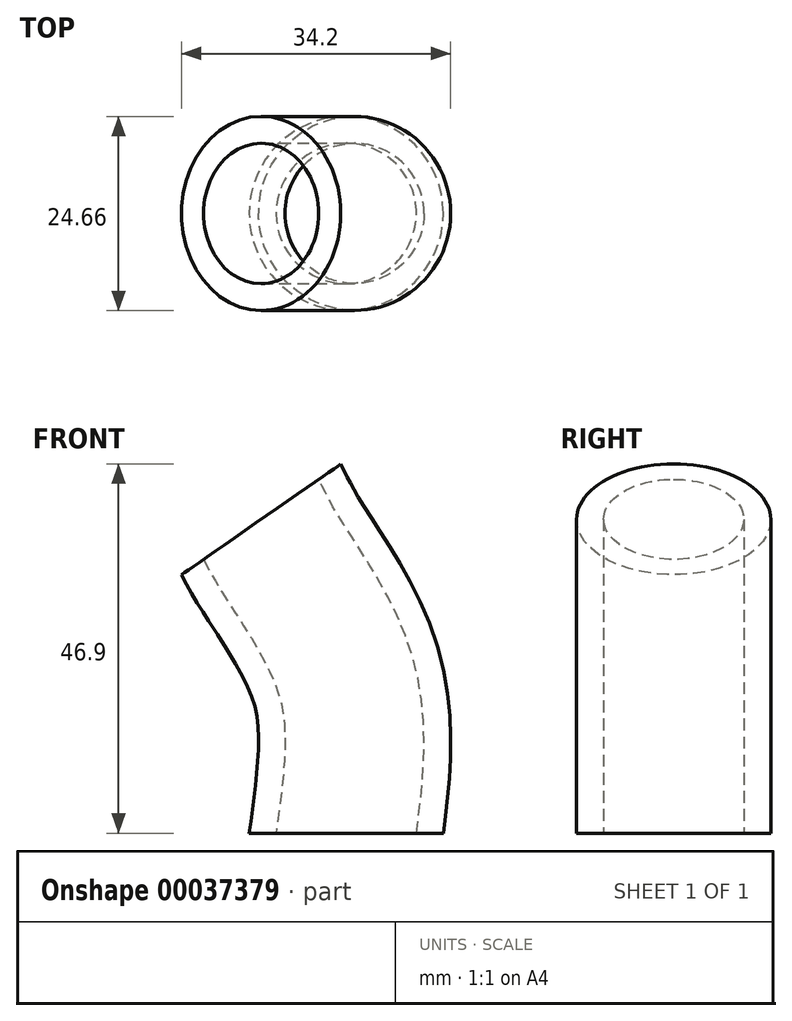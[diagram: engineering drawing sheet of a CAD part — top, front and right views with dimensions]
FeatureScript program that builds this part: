
annotation { "Feature Type Name" : "Feature", "Feature Type Description" : "" }
export const myFeature = defineFeature(function(context is Context, id is Id, definition is map)
    precondition{}
    {
        {
            var Q0;
            Q0=qCreatedBy(makeId("Top.planeOp"),FACE);
            var sketch = newSketch(context, id + "F0", { "sketchPlane" : qUnion([Q0])});
            skCircle(sketch, "E0", {"center": v(0, 0) * mm, "radius": 8.91 * mm});
            skCircle(sketch, "E1", {"center": v(0, 0) * mm, "radius": 12.33 * mm});
            skSolve(sketch);
        }
        {
            var Q0;
            Q0=qCreatedBy(makeId("Front.planeOp"),FACE);
            var sketch = newSketch(context, id + "F1", { "sketchPlane" : qUnion([Q0])});
            skFitSpline(sketch, "E2", {"points": [v(0, 0) * mm, v(0, 19.69) * mm, v(-7.9, 34.7) * mm, v(-10.81, 39.86) * mm], "startDerivative": vector(6.62, 49.73) * mm, "endDerivative": vector(-10.49, 20.37) * mm});
            skSolve(sketch);
        }
        {
            var Q0;
            Q0=makeQuery(id+"F0.imprint","IMPRINT",FACE,{"disambiguationData":[TD([[makeQuery(id+"F0.imprint","IMPRINT",EDGE,{"derivedFrom":sQuery(id+"F0.wireOp",EDGE,"E0")}),-1.0]])]});
            var Q1;
            Q1=sQuery(id+"F1.wireOp",EDGE,"E2");
            sweep(context, id + "F2", {"profiles" : qUnion([Q0]), "path" : qUnion([Q1])});
        }
    });
